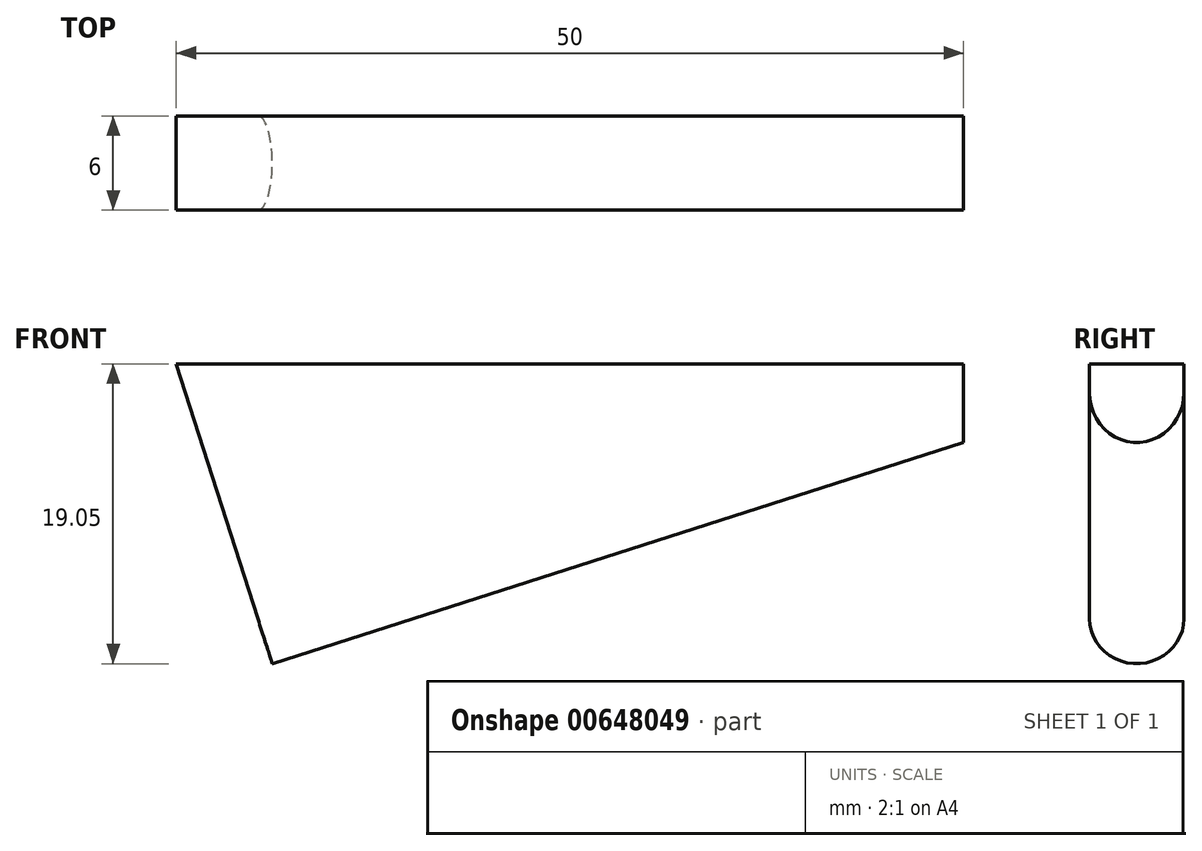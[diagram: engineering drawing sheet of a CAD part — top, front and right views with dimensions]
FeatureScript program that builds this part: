
annotation { "Feature Type Name" : "Feature", "Feature Type Description" : "" }
export const myFeature = defineFeature(function(context is Context, id is Id, definition is map)
    precondition{}
    {
        {
            var Q0;
            Q0=qCreatedBy(makeId("Front.planeOp"),FACE);
            var sketch = newSketch(context, id + "F0", { "sketchPlane" : qUnion([Q0])});
            skLineSegment(sketch, "E0", {"start": v(0, 0) * mm, "end": v(6.1, -19.05) * mm});
            skLineSegment(sketch, "E1", {"start": v(6.1, -19.05) * mm, "end": v(50, -5) * mm});
            skLineSegment(sketch, "E2", {"start": v(50, -5) * mm, "end": v(50, 0) * mm});
            skLineSegment(sketch, "E3", {"start": v(50, 0) * mm, "end": v(0, 0) * mm});
            skSolve(sketch);
        }
        {
            var Q0;
            Q0 = qSketchRegion(id + "F0", true);
            extrude(context, id + "F1", {"entities" : qUnion([Q0]), "endBound" : BoundingType.SYMMETRIC, "depth" : 6 * mm, "offsetDistance" : 25 * mm});
        }
        {
            var Q0;
            Q0=makeQuery(id+"F1.opExtrude","CAP_EDGE",EDGE,{"disambiguationData":[OSD([sQuery(id+"F0.wireOp",EDGE,"E1")])],"isStart":false});
            var Q1;
            Q1=makeQuery(id+"F1.opExtrude","CAP_EDGE",EDGE,{"disambiguationData":[OSD([sQuery(id+"F0.wireOp",EDGE,"E1")])],"isStart":true});
            fillet(context, id + "F2", {"entities" : qUnion([Q0, Q1]), "radius" : 3 * mm, "tangentPropagation" : true, "allowEdgeOverflow" : false});
        }
    });
